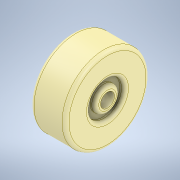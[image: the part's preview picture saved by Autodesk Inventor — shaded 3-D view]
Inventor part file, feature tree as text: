
AUTODESK INVENTOR PART (.ipt)
format: ipt  version: 2022.1 (Build 261234000, 234)  size: 194,560 bytes
history: native  units: mm
features: extrude x4, sketch x4, fillet x3, other x1
ambient origin geometry x8: Origin, YZ Plane, XZ Plane, XY Plane, X Axis, Y Axis, Z Axis, Center Point
bodies: Body1 (feature_tree)
feature tree (12):
  other  "Sólido1"
  extrude  "Extrusión1"  Depth=50.0mm TaperAngle=0.0deg
  sketch  "Boceto2"  dims[d4=5.0mm d5=35.0mm d6=7.5mm d7=0.0mm]
  fillet  "Empalme1"  Radius=50.0mm
  extrude  "Extrusión2"  Depth=35.0mm
  fillet  "Empalme2"  Radius=7.5mm
  extrude  "Extrusión3"  Depth=7.5mm TaperAngle=0.0deg
  fillet  "Empalme3"  Radius=5.0mm
  extrude  "Extrusión4"  Depth=20.0mm
  sketch  "Boceto1"  dims[d0=120.0mm d1=50.0mm d2=0.0mm d3=50.0mm]
  sketch  "Boceto3"  dims[d8=5.0mm d10=7.5mm d11=0.0mm d12=5.0mm]
  sketch  "Boceto4"  dims[d13=0.0mm d14=0.0mm d15=20.0mm d9=0.872665mm]
